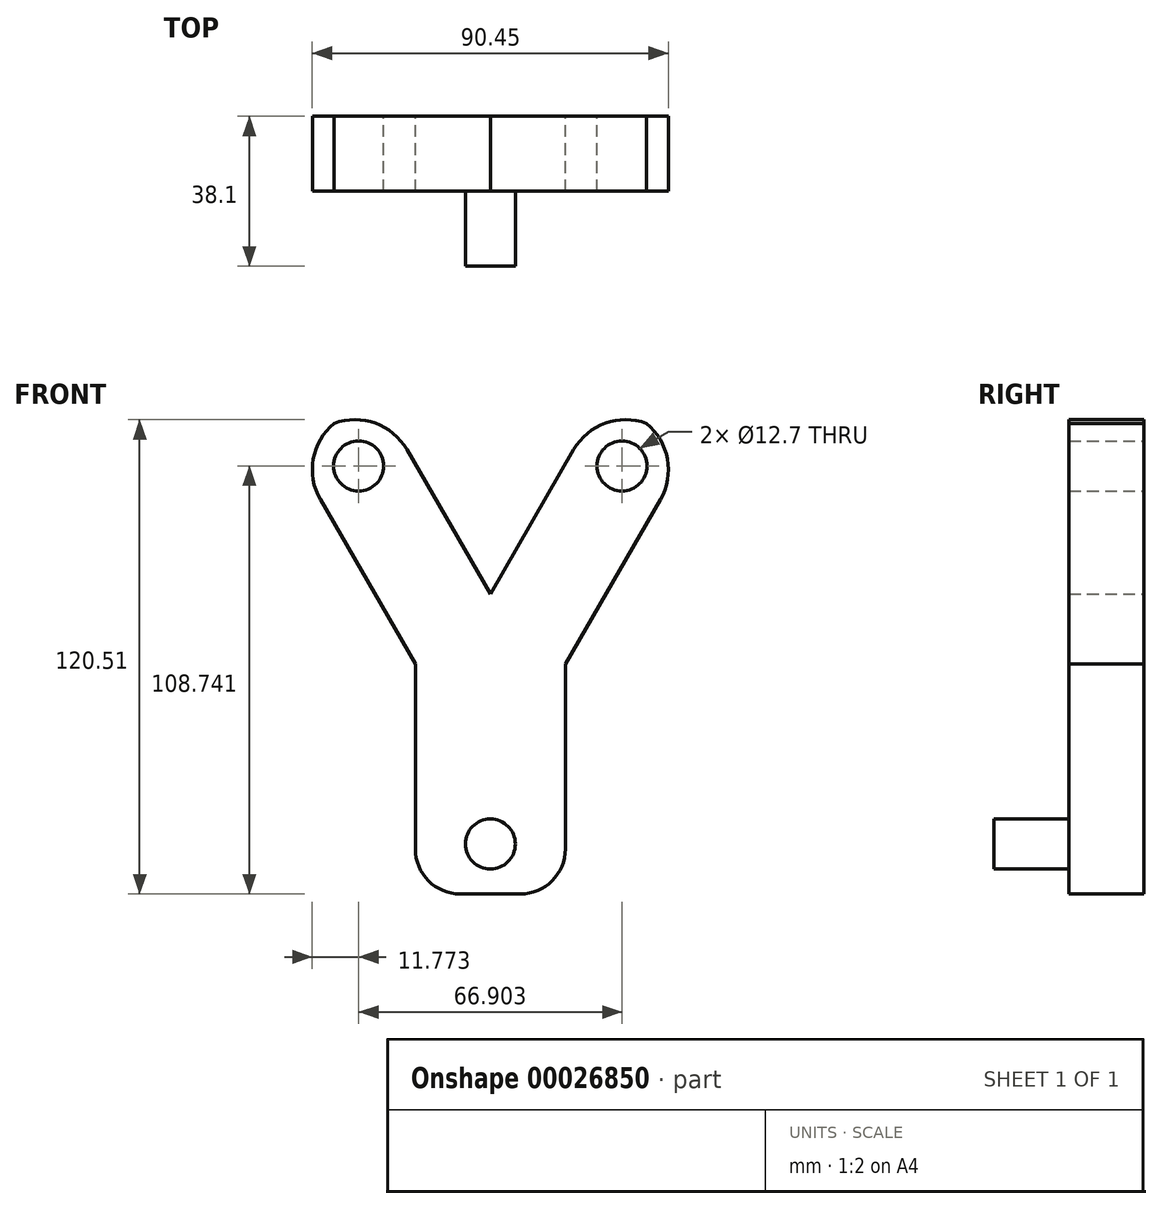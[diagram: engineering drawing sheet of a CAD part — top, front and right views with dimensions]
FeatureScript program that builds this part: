
annotation { "Feature Type Name" : "Feature", "Feature Type Description" : "" }
export const myFeature = defineFeature(function(context is Context, id is Id, definition is map)
    precondition{}
    {
        {
            var Q0;
            Q0=qCreatedBy(makeId("Front.planeOp"),FACE);
            var sketch = newSketch(context, id + "F0", { "sketchPlane" : qUnion([Q0])});
            skLineSegment(sketch, "E0.top", {"start": v(-33.28, -74.33) * mm, "end": v(-18.04, -74.33) * mm});
            skLineSegment(sketch, "E0.left", {"start": v(-44.7, -15.93) * mm, "end": v(-44.7, -62.9) * mm});
            skLineSegment(sketch, "E0.right", {"start": v(-6.6, -15.93) * mm, "end": v(-6.6, -62.9) * mm});
            skLineSegment(sketch, "E1", {"start": v(-44.7, -15.93) * mm, "end": v(-68.84, 25.86) * mm});
            skLineSegment(sketch, "E2", {"start": v(-67.66, 44.14) * mm, "end": v(-63.26, 46.68) * mm});
            skLineSegment(sketch, "E3", {"start": v(-46.84, 38.56) * mm, "end": v(-25.66, 1.87) * mm});
            skLineSegment(sketch, "E4", {"start": v(-6.6, -15.93) * mm, "end": v(17.52, 25.86) * mm});
            skLineSegment(sketch, "E5", {"start": v(16.35, 44.14) * mm, "end": v(11.95, 46.68) * mm});
            skLineSegment(sketch, "E6", {"start": v(-4.47, 38.56) * mm, "end": v(-25.66, 1.87) * mm});
            skCircle(sketch, "E7", {"center": v(-59.1, 34.41) * mm, "radius": 6.35 * mm});
            skCircle(sketch, "E8", {"center": v(7.8, 34.41) * mm, "radius": 6.35 * mm});
            skPoint(sketch, "E9.visualSharp", {"position": v(-54.46, 51.76) * mm});
            skArc(sketch, "E9.filletArc", {"start": v(-46.84, 38.56) * mm, "mid": v(-56.1, 45.66) * mm, "end": v(-67.66, 44.14) * mm});
            skPoint(sketch, "E10.visualSharp", {"position": v(-76.46, 39.06) * mm});
            skArc(sketch, "E10.filletArc", {"start": v(-63.26, 46.68) * mm, "mid": v(-70.36, 37.43) * mm, "end": v(-68.84, 25.86) * mm});
            skPoint(sketch, "E11.visualSharp", {"position": v(3.15, 51.76) * mm});
            skArc(sketch, "E11.filletArc", {"start": v(16.35, 44.14) * mm, "mid": v(4.78, 45.66) * mm, "end": v(-4.47, 38.56) * mm});
            skPoint(sketch, "E12.visualSharp", {"position": v(25.14, 39.06) * mm});
            skArc(sketch, "E12.filletArc", {"start": v(17.52, 25.86) * mm, "mid": v(19.05, 37.43) * mm, "end": v(11.95, 46.68) * mm});
            skPoint(sketch, "E13.visualSharp", {"position": v(-44.7, -74.33) * mm});
            skArc(sketch, "E13.filletArc", {"start": v(-44.7, -62.9) * mm, "mid": v(-41.36, -70.98) * mm, "end": v(-33.28, -74.33) * mm});
            skPoint(sketch, "E14.visualSharp", {"position": v(-6.6, -74.33) * mm});
            skArc(sketch, "E14.filletArc", {"start": v(-18.04, -74.33) * mm, "mid": v(-9.95, -70.98) * mm, "end": v(-6.6, -62.9) * mm});
            skCircle(sketch, "E15", {"center": v(-25.66, -61.63) * mm, "radius": 6.35 * mm});
            skSolve(sketch);
        }
        {
            var Q0;
            Q0=makeQuery(id+"F0.imprint","IMPRINT",FACE,{"disambiguationData":[TD([[makeQuery(id+"F0.imprint","IMPRINT",EDGE,{"derivedFrom":sQuery(id+"F0.wireOp",EDGE,"E0.top")}),1.0]])]});
            extrude(context, id + "F1", {"entities" : qUnion([Q0]), "depth" : 19.05 * mm});
        }
        {
            var Q0;
            Q0=makeQuery(id+"F0.imprint","IMPRINT",FACE,{"disambiguationData":[TD([[makeQuery(id+"F0.imprint","IMPRINT",EDGE,{"derivedFrom":sQuery(id+"F0.wireOp",EDGE,"E15")}),1.0]])]});
            extrude(context, id + "F2", {"entities" : qUnion([Q0]), "operationType" : NewBodyOperationType.ADD, "depth" : 38.1 * mm});
        }
    });
